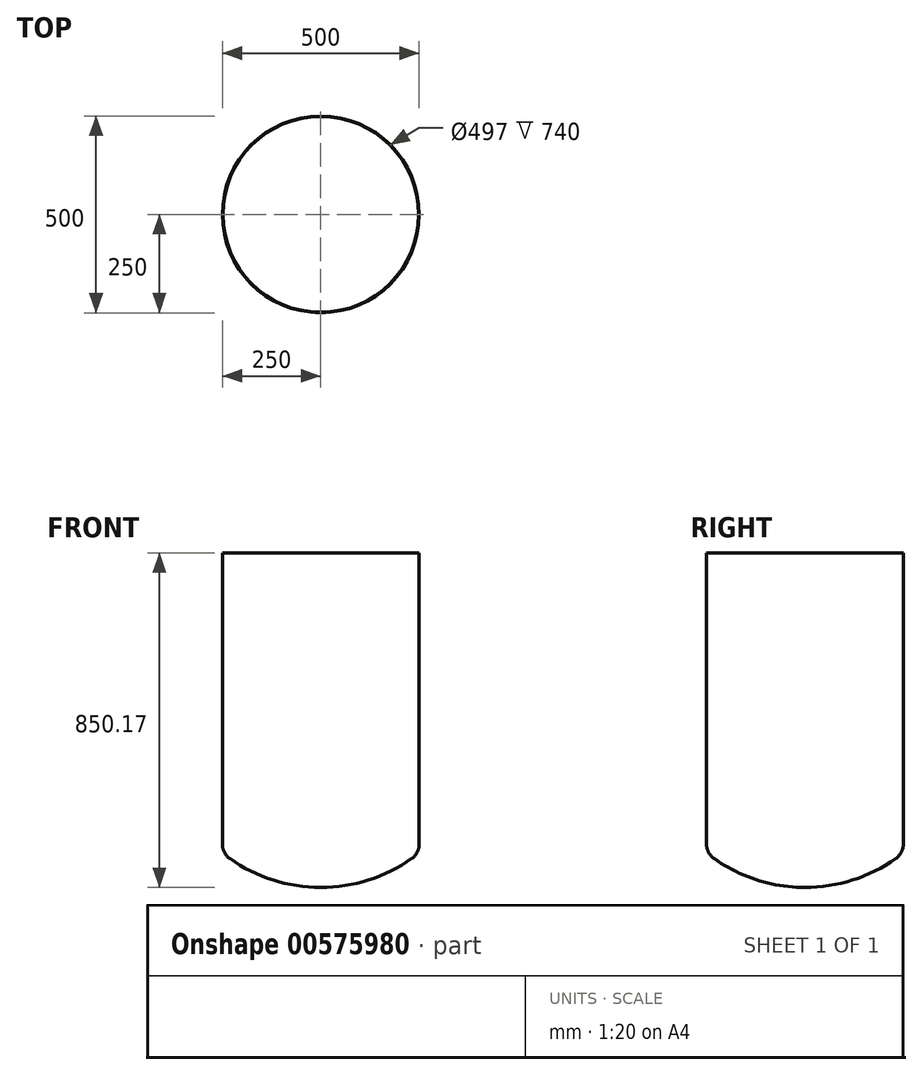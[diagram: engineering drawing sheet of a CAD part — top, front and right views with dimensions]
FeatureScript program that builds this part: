
annotation { "Feature Type Name" : "Feature", "Feature Type Description" : "" }
export const myFeature = defineFeature(function(context is Context, id is Id, definition is map)
    precondition{}
    {
        {
            var Q0;
            Q0=qCreatedBy(makeId("Right.planeOp"),FACE);
            var sketch = newSketch(context, id + "F0", { "sketchPlane" : qUnion([Q0])});
            skLineSegment(sketch, "E0", {"start": v(0, 192.5) * mm, "end": v(0, -214.32) * mm, "construction": true});
            skArc(sketch, "E1", {"start": v(-230.99, 73.43) * mm, "mid": v(-121.19, 18.8) * mm, "end": v(0, 0) * mm});
            skArc(sketch, "E2", {"start": v(-250, 110.17) * mm, "mid": v(-244.96, 89.49) * mm, "end": v(-230.99, 73.43) * mm});
            skLineSegment(sketch, "E3", {"start": v(-250, 150.17) * mm, "end": v(-250, 110.17) * mm});
            skLineSegment(sketch, "E4", {"start": v(0, 0) * mm, "end": v(257.23, 0) * mm, "construction": true});
            skLineSegment(sketch, "E5", {"start": v(-250, 150.17) * mm, "end": v(-250, 850.17) * mm});
            skLineSegment(sketch, "E6", {"start": v(-250, 850.17) * mm, "end": v(0, 850.17) * mm});
            skLineSegment(sketch, "E7", {"start": v(0, 850.17) * mm, "end": v(0, 0) * mm});
            skSolve(sketch);
        }
        {
            var Q0;
            Q0=makeQuery(id+"F0.imprint","IMPRINT",FACE,{"disambiguationData":[TD([[makeQuery(id+"F0.imprint","IMPRINT",EDGE,{"derivedFrom":sQuery(id+"F0.wireOp",EDGE,"E1")}),1.0]])]});
            var Q1;
            Q1=sQuery(id+"F0.wireOp",EDGE,"E0");
            revolve(context, id + "F1", {"surfaceOperationType" : NewSurfaceOperationType.NEW, "entities" : qUnion([Q0]), "axis" : qUnion([Q1]), "revolveType" : RevolveType.FULL});
        }
        {
            var Q0;
            Q0=makeQuery(id+"F1.opRevolve","SWEPT_FACE",FACE,{"disambiguationData":[OSD([sQuery(id+"F0.wireOp",EDGE,"E6")])]});
            shell(context, id + "F2", {"entities" : qUnion([Q0]), "thickness" : 1.5 * mm});
        }
    });
